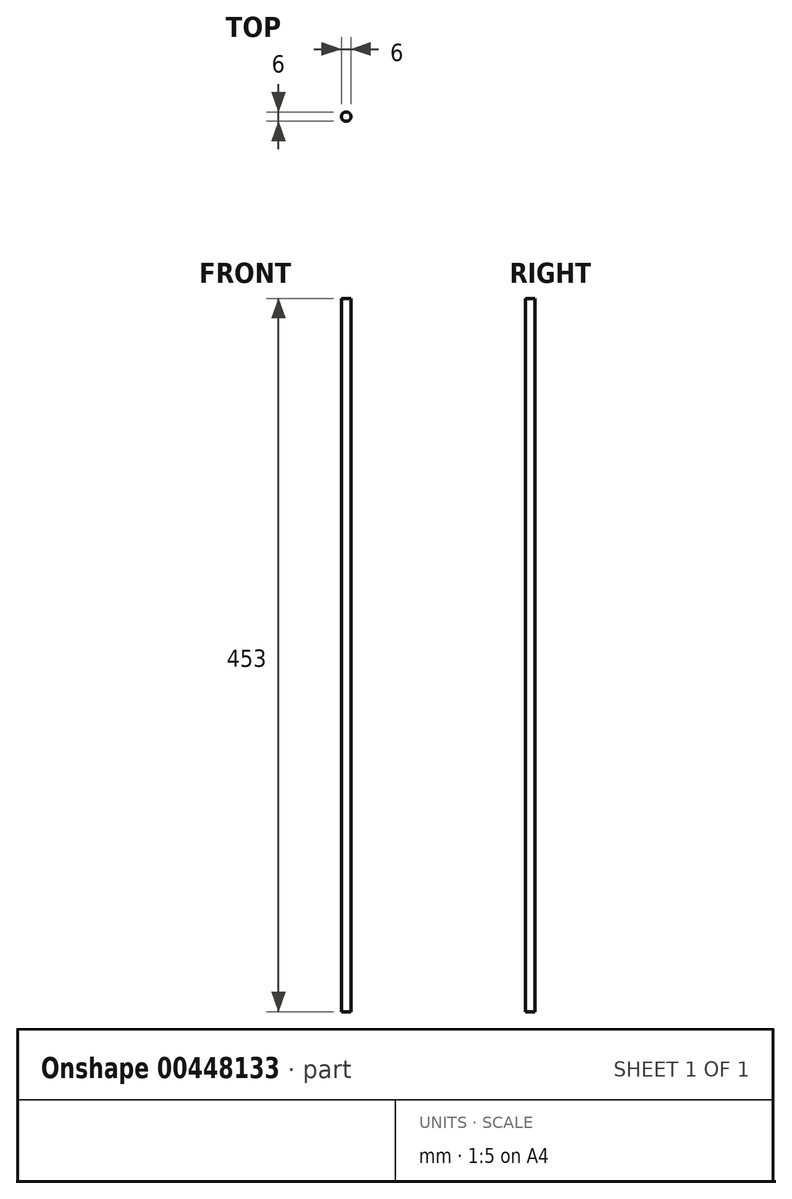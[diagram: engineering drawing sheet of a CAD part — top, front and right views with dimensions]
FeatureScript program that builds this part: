
annotation { "Feature Type Name" : "Feature", "Feature Type Description" : "" }
export const myFeature = defineFeature(function(context is Context, id is Id, definition is map)
    precondition{}
    {
        {
            var Q0;
            Q0=qCreatedBy(makeId("Top.planeOp"),FACE);
            var sketch = newSketch(context, id + "F0", { "sketchPlane" : qUnion([Q0])});
            skCircle(sketch, "E0", {"center": v(0, 0) * mm, "radius": 3 * mm});
            skSolve(sketch);
        }
        {
            var Q0;
            Q0 = qSketchRegion(id + "F0", true);
            extrude(context, id + "F1", {"entities" : qUnion([Q0]), "depth" : 453 * mm});
        }
    });
